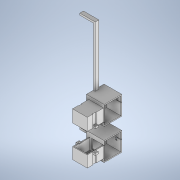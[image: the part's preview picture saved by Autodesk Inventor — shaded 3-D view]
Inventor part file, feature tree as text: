
AUTODESK INVENTOR PART (.ipt)
format: ipt  version: 2020.2 (Build 242310000, 310)  size: 762,880 bytes
history: native  units: mm
features: sketch x35, extrude x34, projected_geometry x11, hole x2
ambient origin geometry x8: Origin, YZ Plane, XZ Plane, XY Plane, X Axis, Y Axis, Z Axis, Center Point
bodies: Solid1 (feature_tree)
feature tree (82):
  sketch  "Sketch1"  dims[d0=29.0mm d1=35.0mm]
  extrude  "Extrusion1"  Depth=35.0mm
  extrude  "Extrusion2"  Depth=2.0mm
  extrude  "Extrusion3"  Depth=39.0mm
  hole  "Hole1"  [1 undecoded]
  extrude  "Extrusion4"  Depth=10.0mm
  sketch  "Sketch5"  dims[d10=10.0mm d11=0.0mm d12=4.2mm]
  sketch  "Sketch6"  dims[d13=4.475mm d14=26.05mm]
  extrude  "Extrusion5"  Depth=26.05mm
  extrude  "Extrusion6"  Depth=39.0mm
  extrude  "Extrusion7"  Depth=33.0mm TaperAngle=0.0deg
  sketch  "Sketch10"  dims[d27=7.0mm d28=7.0mm]
  extrude  "Extrusion8"  Depth=7.0mm
  extrude  "Extrusion9"  Depth=7.0mm
  extrude  "Extrusion14"  Depth=10.0mm
  extrude  "Extrusion15"  Depth=20.0mm
  extrude  "Extrusion16"  Depth=22.5mm
  extrude  "Extrusion17"  Depth=1.0mm
  extrude  "Extrusion18"  Depth=24.0mm
  extrude  "Extrusion19"  Depth=1.0mm
  extrude  "Extrusion25"  Depth=26.0mm
  extrude  "Extrusion26"  Depth=1.0mm
  extrude  "Extrusion27"  Depth=1.0mm
  extrude  "Extrusion28"  Depth=26.0mm TaperAngle=0.0deg
  extrude  "Extrusion29"  Depth=1.0mm TaperAngle=0.0deg
  extrude  "Extrusion30"  Depth=14.0mm
  extrude  "Extrusion31"  TaperAngle=90.0deg  [1 undecoded]
  extrude  "Extrusion32"  Depth=3.5mm
  sketch  "Sketch39"  dims[d82=35.0mm d83=3.5mm]
  extrude  "Extrusion33"  Depth=7.0mm
  extrude  "Extrusion34"  Depth=7.0mm
  extrude  "Extrusion37"  Depth=5.0mm TaperAngle=0.0deg
  extrude  "Extrusion38"  Depth=1.0mm TaperAngle=0.0deg
  sketch  "Sketch43"  dims[d88=3.4mm d89=5.0mm d90=0.0mm]
  extrude  "Extrusion39"  Depth=1.0mm TaperAngle=0.0deg
  extrude  "Extrusion40"  Depth=16.0mm
  extrude  "Extrusion42"  Depth=1.5mm
  extrude  "Extrusion43"  Depth=5.0mm
  hole  "Hole2"  [1 undecoded]
  extrude  "Extrusion44"  Depth=21.0mm
  extrude  "Extrusion45"  Depth=19.5mm
  extrude  "Extrusion46"  Depth=4.0mm
  sketch  "Sketch2"  dims[d2=2.0mm d3=2.0mm]
  sketch  "Sketch3"  dims[d4=33.0mm d5=39.0mm]
  sketch  "Sketch4"  dims[d6=2.0mm d7=0.0mm d8=40.0mm d9=0.0mm]
  sketch  "Sketch7"  dims[d15=29.6mm]
  projected_geometry  "Projected Loop1"
  sketch  "Sketch8"  dims[d16=3.4mm d17=6.0mm d18=6.3mm d19=2.0mm d20=90.0deg d21=8.0mm d22=20.594885mm d23=39.0mm]
  sketch  "Sketch9"  dims[d24=2.0mm d25=33.0mm d26=0.0mm]
  sketch  "Sketch11"  dims[d29=7.0mm d30=7.0mm]
  sketch  "Sketch16"  dims[d31=5.0mm d32=0.0mm d33=10.0mm]
  sketch  "Sketch17"  dims[d34=3.5mm d35=20.0mm]
  sketch  "Sketch18"  dims[d36=90.0deg d37=22.5mm]
  projected_geometry  "Projected Loop4"
  sketch  "Sketch19"  dims[d38=10.0mm d39=0.0mm d40=1.0mm]
  projected_geometry  "Projected Loop5"
  sketch  "Sketch21"  dims[d41=10.0mm d42=0.0mm d43=24.0mm]
  projected_geometry  "Projected Loop6"
  sketch  "Sketch30"  dims[d44=30.48mm d45=1.0mm]
  projected_geometry  "Projected Loop7"
  sketch  "Sketch31"  dims[d46=31.48mm d47=26.0mm]
  projected_geometry  "Projected Loop8"
  sketch  "Sketch32"  dims[d48=34.0mm d49=0.0mm d50=1.0mm]
  projected_geometry  "Projected Loop9"
  projected_geometry  "Projected Loop10"
  sketch  "Sketch34"  dims[d51=29.48mm d52=0.0mm d69=1.0mm]
  sketch  "Sketch35"  dims[d70=35.0mm d71=26.0mm d72=0.0mm]
  sketch  "Sketch36"  dims[d73=10.0mm d74=0.0mm d75=1.0mm d76=0.0mm]
  sketch  "Sketch37"  dims[d77=1.0mm d78=0.0mm d79=14.0mm]
  sketch  "Sketch38"  dims[d80=17.5mm d81=90.0deg]
  projected_geometry  "Projected Loop12"
  sketch  "Sketch40"  dims[d84=7.0mm d85=7.0mm]
  sketch  "Sketch42"  dims[d86=7.0mm d87=3.4mm]
  projected_geometry  "Projected Loop13"
  sketch  "Sketch44"  dims[d91=1.0mm d92=0.0mm d131=1.0mm d132=0.0mm]
  sketch  "Sketch45"  dims[d133=1.0mm d134=0.0mm d135=1.0mm d136=0.0mm]
  sketch  "Sketch46"  dims[d137=1.0mm d138=0.0mm d139=16.0mm]
  sketch  "Sketch47"  dims[d140=10.0mm d141=1.5mm]
  projected_geometry  "Projected Loop14"
  sketch  "Sketch49"  dims[d142=2.0mm d143=5.0mm]
  sketch  "Sketch50"  dims[d144=3.5mm d145=5.5mm]
  sketch  "Sketch51"  dims[d146=10.0mm d147=0.0mm d148=21.0mm d149=19.5mm d150=4.0mm d151=8.0mm d152=4.0mm d153=30.0mm d154=0.0mm d155=4.0mm d156=8.0mm d157=201.358mm d158=0.0mm d159=4.0mm d160=30.0mm d161=0.0mm d162=44.0mm d163=4.0mm d164=39.0mm d165=42.0mm d166=90.0deg d167=39.0mm d168=90.0deg d169=2.0mm d170=2.0mm d171=2.0mm d172=2.0mm d173=4.0mm d174=0.0mm d175=35.0mm d176=0.0mm d177=1.0mm d178=7.0mm d179=25.0mm d180=2.0mm d185=2.0mm d186=36.0mm d187=0.0mm d188=2.0mm d189=28.48mm d190=34.0mm d191=25.0mm d192=0.0mm d193=30.0mm d194=0.0mm d195=5.0mm d196=0.0mm d199=1.0mm d200=0.0mm d201=4.75mm d202=4.2mm d203=26.05mm d204=29.6mm d205=3.4mm d206=6.0mm d207=7.0mm d208=5.0mm d209=90.0deg d210=8.0mm d211=20.594885mm d212=3.0mm d213=0.0mm d214=10.0mm d215=0.0mm d216=2.0mm d217=1.0mm d218=32.0mm d219=0.0mm d220=15.0mm d221=10.0mm d222=2.0mm d223=90.0deg d224=6.5mm d225=10.0mm d226=0.0mm d54=0.5mm d55=0.872665mm d56=0.5mm d57=0.872665mm d58=0.5mm d59=0.872665mm d60=0.5mm d61=0.872665mm d116=0.5mm d117=0.872665mm d118=0.5mm d119=0.872665mm]
note: 3 required parameter values undecoded (feature->parameter linkage not recoverable at this tier; creation-order binding heuristic only, values carry confidence <= 0.55)
